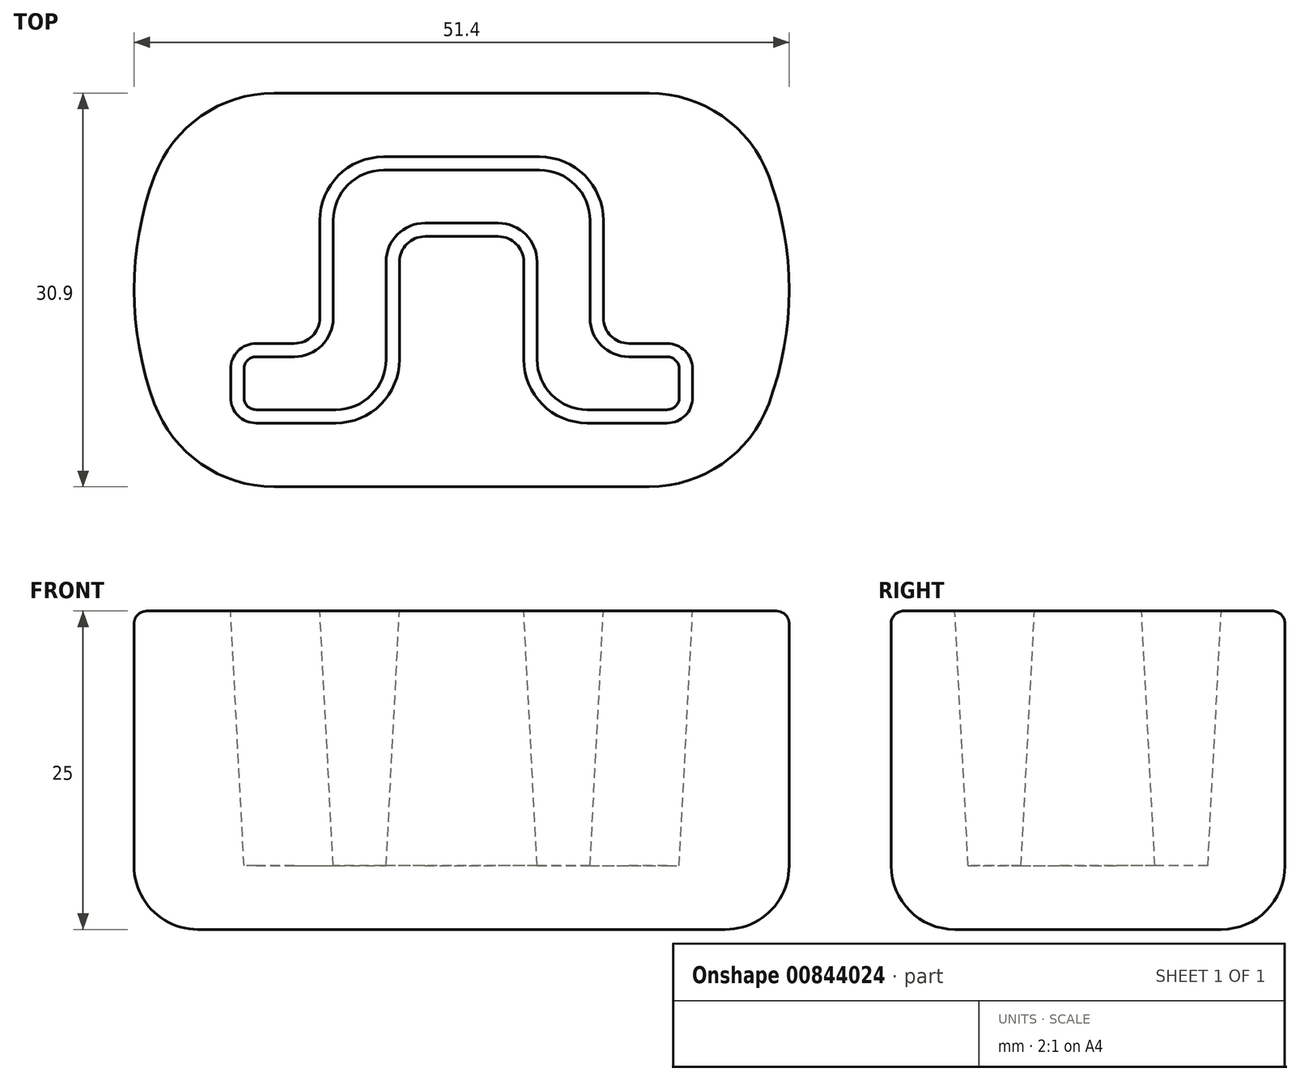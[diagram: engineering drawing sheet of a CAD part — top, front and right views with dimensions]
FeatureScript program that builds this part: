
annotation { "Feature Type Name" : "Feature", "Feature Type Description" : "" }
export const myFeature = defineFeature(function(context is Context, id is Id, definition is map)
    precondition{}
    {
        {
            var Q0;
            Q0=qCreatedBy(makeId("Top.planeOp"),FACE);
            var sketch = newSketch(context, id + "F0", { "sketchPlane" : qUnion([Q0])});
            skLineSegment(sketch, "E0.bottom", {"start": v(6.12, 10.45) * mm, "end": v(-6.12, 10.45) * mm});
            skLineSegment(sketch, "E0.top", {"start": v(16.12, -10.45) * mm, "end": v(9.87, -10.45) * mm});
            skLineSegment(sketch, "E0.left", {"start": v(18.12, -6.2) * mm, "end": v(18.12, -8.45) * mm});
            skLineSegment(sketch, "E0.right", {"start": v(-18.12, -6.2) * mm, "end": v(-18.12, -8.45) * mm});
            skPoint(sketch, "E0.middle", {"position": v(0, 0) * mm});
            skLineSegment(sketch, "E1.0", {"start": v(16.12, -4.2) * mm, "end": v(13.12, -4.2) * mm});
            skLineSegment(sketch, "E2.0", {"start": v(-11.13, 5.45) * mm, "end": v(-11.12, -2.2) * mm});
            skLineSegment(sketch, "E3.0", {"start": v(11.12, 5.45) * mm, "end": v(11.12, -2.2) * mm});
            skLineSegment(sketch, "E4.0", {"start": v(-4.87, 2.2) * mm, "end": v(-4.87, -5.45) * mm});
            skLineSegment(sketch, "E5.0", {"start": v(4.87, 2.2) * mm, "end": v(4.87, -5.45) * mm});
            skPoint(sketch, "E6.orphan", {"position": v(18.12, 10.45) * mm});
            skLineSegment(sketch, "E7.trimOffspring", {"start": v(2.87, 4.2) * mm, "end": v(-2.87, 4.2) * mm});
            skLineSegment(sketch, "E8.trimOffspring", {"start": v(-13.12, -4.2) * mm, "end": v(-16.12, -4.2) * mm});
            skLineSegment(sketch, "E9.trimOffspring", {"start": v(-9.88, -10.45) * mm, "end": v(-16.12, -10.45) * mm});
            skPoint(sketch, "E10.orphan", {"position": v(-18.13, 10.45) * mm});
            skPoint(sketch, "E11.visualSharp", {"position": v(-4.87, -10.45) * mm});
            skArc(sketch, "E11.filletArc", {"start": v(-9.88, -10.45) * mm, "mid": v(-6.34, -8.99) * mm, "end": v(-4.88, -5.45) * mm});
            skPoint(sketch, "E12.visualSharp", {"position": v(4.87, -10.45) * mm});
            skArc(sketch, "E12.filletArc", {"start": v(4.87, -5.45) * mm, "mid": v(6.34, -8.99) * mm, "end": v(9.87, -10.45) * mm});
            skPoint(sketch, "E13.visualSharp", {"position": v(-11.13, 10.45) * mm});
            skArc(sketch, "E13.filletArc", {"start": v(-6.12, 10.45) * mm, "mid": v(-9.66, 8.99) * mm, "end": v(-11.12, 5.45) * mm});
            skPoint(sketch, "E14.visualSharp", {"position": v(11.12, 10.45) * mm});
            skArc(sketch, "E14.filletArc", {"start": v(11.12, 5.45) * mm, "mid": v(9.66, 8.99) * mm, "end": v(6.12, 10.45) * mm});
            skPoint(sketch, "E15.visualSharp", {"position": v(-18.12, -4.2) * mm});
            skArc(sketch, "E15.filletArc", {"start": v(-16.12, -4.2) * mm, "mid": v(-17.54, -4.79) * mm, "end": v(-18.13, -6.2) * mm});
            skPoint(sketch, "E16.visualSharp", {"position": v(-18.12, -10.45) * mm});
            skArc(sketch, "E16.filletArc", {"start": v(-18.12, -8.45) * mm, "mid": v(-17.54, -9.86) * mm, "end": v(-16.12, -10.45) * mm});
            skPoint(sketch, "E17.visualSharp", {"position": v(18.13, -10.45) * mm});
            skArc(sketch, "E17.filletArc", {"start": v(16.12, -10.45) * mm, "mid": v(17.54, -9.86) * mm, "end": v(18.13, -8.45) * mm});
            skPoint(sketch, "E18.visualSharp", {"position": v(18.12, -4.2) * mm});
            skArc(sketch, "E18.filletArc", {"start": v(18.13, -6.2) * mm, "mid": v(17.54, -4.79) * mm, "end": v(16.12, -4.2) * mm});
            skPoint(sketch, "E19.visualSharp", {"position": v(-11.12, -4.2) * mm});
            skArc(sketch, "E19.filletArc", {"start": v(-13.12, -4.2) * mm, "mid": v(-11.71, -3.61) * mm, "end": v(-11.12, -2.2) * mm});
            skPoint(sketch, "E20.visualSharp", {"position": v(11.12, -4.2) * mm});
            skArc(sketch, "E20.filletArc", {"start": v(11.12, -2.2) * mm, "mid": v(11.71, -3.61) * mm, "end": v(13.12, -4.2) * mm});
            skPoint(sketch, "E21.visualSharp", {"position": v(-4.88, 4.2) * mm});
            skArc(sketch, "E21.filletArc", {"start": v(-2.88, 4.2) * mm, "mid": v(-4.29, 3.61) * mm, "end": v(-4.87, 2.2) * mm});
            skPoint(sketch, "E22.visualSharp", {"position": v(4.87, 4.2) * mm});
            skArc(sketch, "E22.filletArc", {"start": v(4.87, 2.2) * mm, "mid": v(4.29, 3.61) * mm, "end": v(2.87, 4.2) * mm});
            skArc(sketch, "E23", {"start": v(-24.1, 8.92) * mm, "mid": v(-25.7, 0) * mm, "end": v(-24.1, -8.92) * mm});
            skLineSegment(sketch, "E24.0", {"start": v(14.72, 15.45) * mm, "end": v(-14.72, 15.45) * mm});
            skLineSegment(sketch, "E25.0", {"start": v(14.72, -15.45) * mm, "end": v(-14.72, -15.45) * mm});
            skArc(sketch, "E26.trimOffspring", {"start": v(24.1, -8.92) * mm, "mid": v(25.7, 0) * mm, "end": v(24.1, 8.92) * mm});
            skPoint(sketch, "E27.visualSharp", {"position": v(-20.54, 15.45) * mm});
            skArc(sketch, "E27.filletArc", {"start": v(-14.72, 15.45) * mm, "mid": v(-20.44, 13.66) * mm, "end": v(-24.1, 8.92) * mm});
            skPoint(sketch, "E28.visualSharp", {"position": v(-20.54, -15.45) * mm});
            skArc(sketch, "E28.filletArc", {"start": v(-24.1, -8.92) * mm, "mid": v(-20.44, -13.66) * mm, "end": v(-14.72, -15.45) * mm});
            skPoint(sketch, "E29.visualSharp", {"position": v(20.54, 15.45) * mm});
            skArc(sketch, "E29.filletArc", {"start": v(24.1, 8.92) * mm, "mid": v(20.44, 13.66) * mm, "end": v(14.72, 15.45) * mm});
            skPoint(sketch, "E30.visualSharp", {"position": v(20.54, -15.45) * mm});
            skArc(sketch, "E30.filletArc", {"start": v(14.72, -15.45) * mm, "mid": v(20.44, -13.66) * mm, "end": v(24.1, -8.92) * mm});
            skSolve(sketch);
        }
        {
            var Q0;
            Q0=makeQuery(id+"F0.imprint","IMPRINT",FACE,{"disambiguationData":[TD([[makeQuery(id+"F0.imprint","IMPRINT",EDGE,{"derivedFrom":sQuery(id+"F0.wireOp",EDGE,"E0.bottom")}),-1.0]])]});
            var Q1;
            Q1=makeQuery(id+"F0.imprint","IMPRINT",FACE,{"disambiguationData":[TD([[makeQuery(id+"F0.imprint","IMPRINT",EDGE,{"derivedFrom":sQuery(id+"F0.wireOp",EDGE,"E0.bottom")}),1.0]])]});
            extrude(context, id + "F1", {"entities" : qUnion([Q0, Q1]), "oppositeDirection" : true, "depth" : 25 * mm, "offsetDistance" : 25 * mm});
        }
        {
            var Q0;
            Q0=makeQuery(id+"F0.imprint","IMPRINT",FACE,{"disambiguationData":[TD([[makeQuery(id+"F0.imprint","IMPRINT",EDGE,{"derivedFrom":sQuery(id+"F0.wireOp",EDGE,"E0.bottom")}),1.0]])]});
            extrude(context, id + "F2", {"entities" : qUnion([Q0]), "operationType" : NewBodyOperationType.REMOVE, "oppositeDirection" : true, "depth" : 20 * mm, "offsetDistance" : 25 * mm, "hasDraft" : true, "draftAngle" : 3 * degree, "draftPullDirection" : true});
        }
        {
            var Q0;
            Q0=makeQuery(id+"F1.opExtrude","CAP_EDGE",EDGE,{"disambiguationData":[OSD([sQuery(id+"F0.wireOp",EDGE,"E25.0")])],"isStart":true});
            fillet(context, id + "F3", {"entities" : qUnion([Q0]), "radius" : 1 * mm, "tangentPropagation" : true, "allowEdgeOverflow" : false});
        }
        {
            var Q0;
            Q0=makeQuery(id+"F1.opExtrude","CAP_EDGE",EDGE,{"disambiguationData":[OSD([sQuery(id+"F0.wireOp",EDGE,"E25.0")])],"isStart":false});
            fillet(context, id + "F4", {"entities" : qUnion([Q0]), "radius" : 5 * mm, "tangentPropagation" : true, "allowEdgeOverflow" : false});
        }
    });
